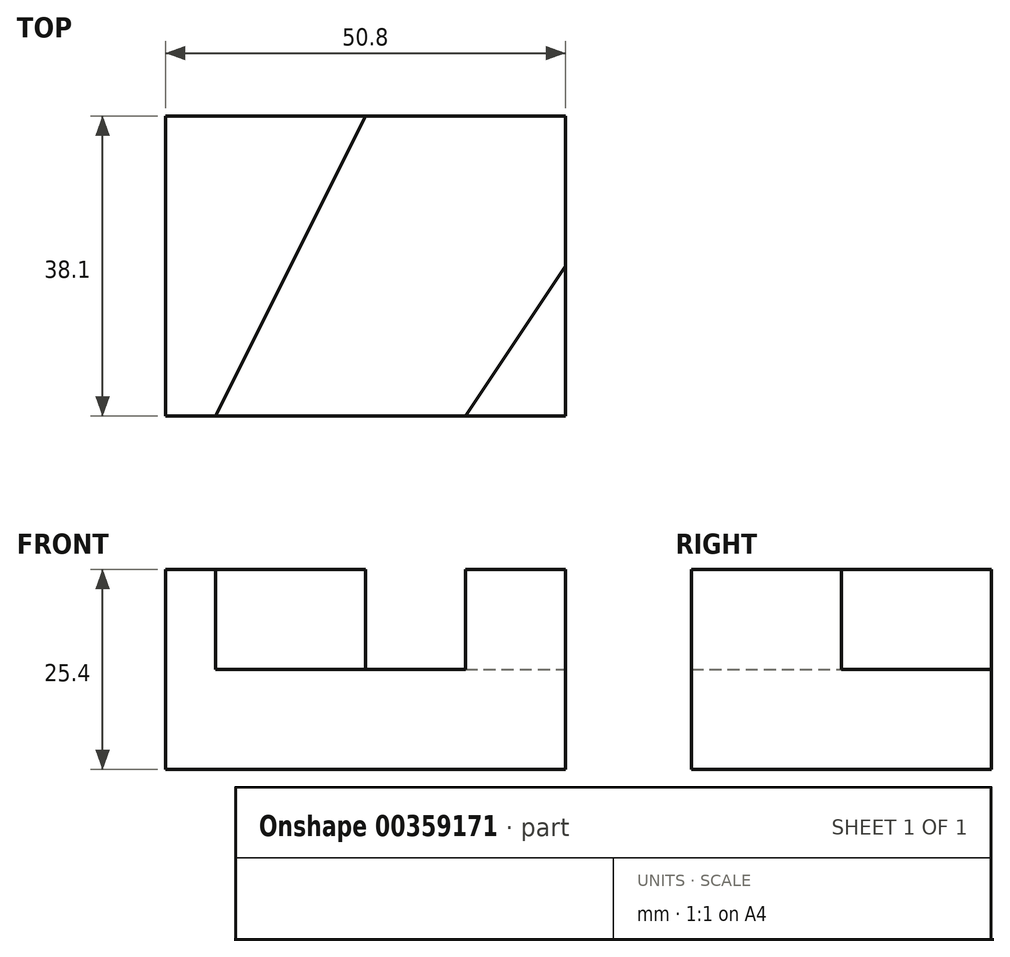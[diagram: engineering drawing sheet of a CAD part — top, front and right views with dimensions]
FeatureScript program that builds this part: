
annotation { "Feature Type Name" : "Feature", "Feature Type Description" : "" }
export const myFeature = defineFeature(function(context is Context, id is Id, definition is map)
    precondition{}
    {
        {
            var Q0;
            Q0=qCreatedBy(makeId("Front.planeOp"),FACE);
            var sketch = newSketch(context, id + "F0", { "sketchPlane" : qUnion([Q0])});
            skLineSegment(sketch, "E0.bottom", {"start": v(0, 25.4) * mm, "end": v(50.8, 25.4) * mm});
            skLineSegment(sketch, "E0.top", {"start": v(0, 0) * mm, "end": v(50.8, 0) * mm});
            skLineSegment(sketch, "E0.left", {"start": v(0, 25.4) * mm, "end": v(0, 0) * mm});
            skLineSegment(sketch, "E0.right", {"start": v(50.8, 25.4) * mm, "end": v(50.8, 0) * mm});
            skSolve(sketch);
        }
        {
            var Q0;
            Q0 = qSketchRegion(id + "F0", true);
            extrude(context, id + "F1", {"entities" : qUnion([Q0]), "depth" : 38.1 * mm});
        }
        {
            var Q0;
            Q0=makeQuery(id+"F1.opExtrude","SWEPT_FACE",FACE,{"disambiguationData":[OSD([sQuery(id+"F0.wireOp",EDGE,"E0.bottom")])]});
            var sketch = newSketch(context, id + "F2", { "sketchPlane" : qUnion([Q0])});
            skLineSegment(sketch, "E1", {"start": v(6.35, -38.1) * mm, "end": v(25.4, 0) * mm});
            skLineSegment(sketch, "E2", {"start": v(38.1, -38.1) * mm, "end": v(50.8, -19.05) * mm});
            skSolve(sketch);
        }
        {
            var Q0;
            Q0 = qSketchRegion(id + "F2", true);
            var Q1;
            {var subQ5=sQuery(id+"F2.wireOp",EDGE,"E1");Q1=makeQuery(id+"F2.imprint","IMPRINT",FACE,{"disambiguationData":[TD([[makeQuery(id+"F2.imprint","IMPRINT",EDGE,{"derivedFrom":subQ5}),-1.0]])]});}
            extrude(context, id + "F3", {"entities" : qUnion([Q0, Q1]), "operationType" : NewBodyOperationType.REMOVE, "oppositeDirection" : true, "depth" : 12.7 * mm});
        }
    });
